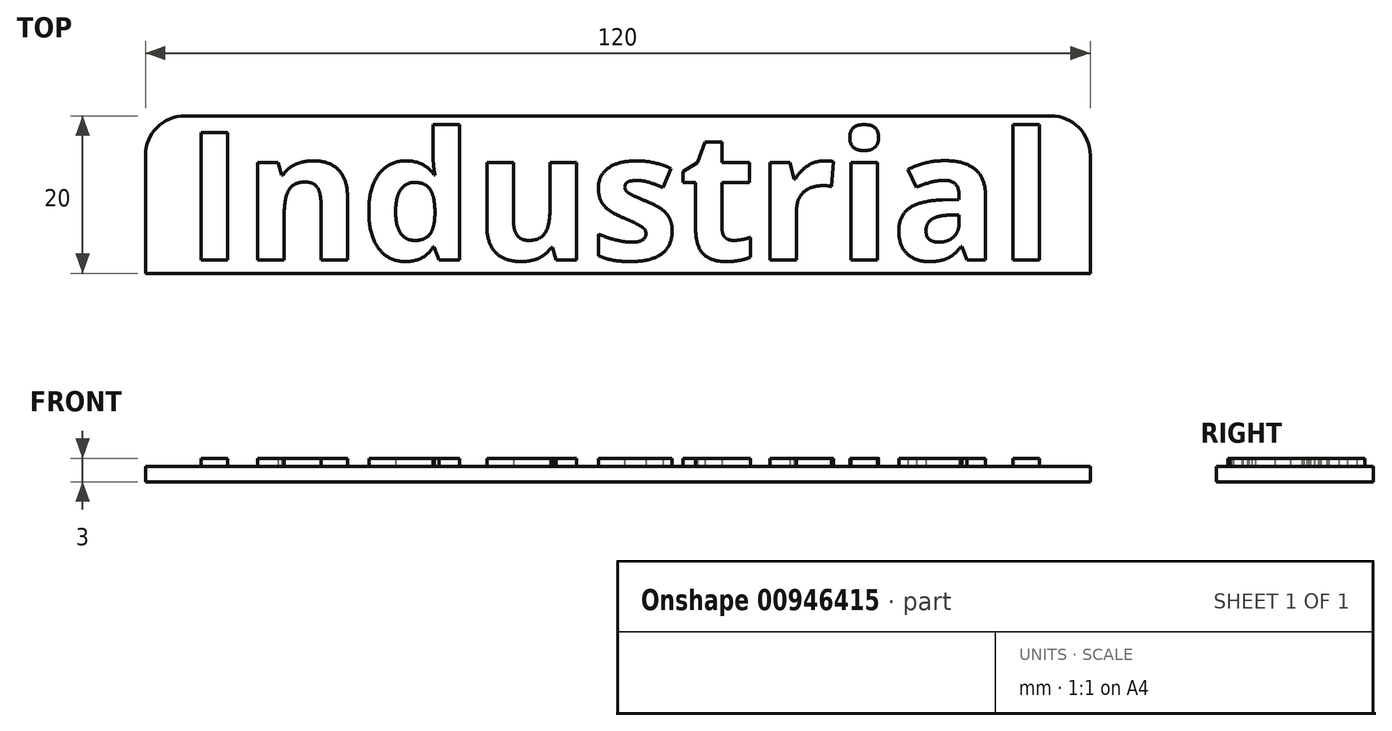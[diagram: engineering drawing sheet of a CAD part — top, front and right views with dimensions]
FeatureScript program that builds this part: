
annotation { "Feature Type Name" : "Feature", "Feature Type Description" : "" }
export const myFeature = defineFeature(function(context is Context, id is Id, definition is map)
    precondition{}
    {
        {
            var Q0;
            Q0=qCreatedBy(makeId("Top.planeOp"),FACE);
            var sketch = newSketch(context, id + "F0", { "sketchPlane" : qUnion([Q0])});
            skLineSegment(sketch, "E0.bottom", {"start": v(-60, 10) * mm, "end": v(60, 10) * mm});
            skLineSegment(sketch, "E0.top", {"start": v(-60, -10) * mm, "end": v(60, -10) * mm});
            skLineSegment(sketch, "E0.left", {"start": v(-60, 10) * mm, "end": v(-60, -10) * mm});
            skLineSegment(sketch, "E0.right", {"start": v(60, 10) * mm, "end": v(60, -10) * mm});
            skPoint(sketch, "E0.middle", {"position": v(0, 0) * mm});
            skSolve(sketch);
        }
        {
            var Q0;
            Q0=qSketchRegion(id+"F0",true);
            extrude(context, id + "F1", {"entities" : qUnion([Q0]), "depth" : 2 * mm, "offsetDistance" : 25 * mm});
        }
        {
            var Q0;
            Q0=makeQuery(id+"F1.opExtrude","CAP_FACE",FACE,{"disambiguationData":[OSD([sQuery(id+"F0.wireOp",EDGE,"E0.bottom"),sQuery(id+"F0.wireOp",EDGE,"E0.top"),sQuery(id+"F0.wireOp",EDGE,"E0.left"),sQuery(id+"F0.wireOp",EDGE,"E0.right")])],"isStart":false});
            var sketch = newSketch(context, id + "F2", { "sketchPlane" : qUnion([Q0])});
            skText(sketch, "E1", { "text": "Industrial\n", "fontName": "OpenSans-Bold.ttf"});
            const initialGuessF2  = {"E1": [-0.055, -0.00828, 1, 0, 0.01628]};
            skSetInitialGuess(sketch, initialGuessF2);
            skSolve(sketch);
        }
        {
            var Q0;
            Q0=qSketchRegion(id+"F2",true);
            extrude(context, id + "F3", {"entities" : qUnion([Q0]), "operationType" : NewBodyOperationType.ADD, "depth" : 1 * mm, "offsetDistance" : 25 * mm});
        }
        {
            var Q0;
            Q0=makeQuery(id+"F1.opExtrude","SWEPT_EDGE",EDGE,{"disambiguationData":[OSD([sQuery(id+"F0.wireOp",EDGE,"E0.bottom"),sQuery(id+"F0.wireOp",EDGE,"E0.left")])]});
            var Q1;
            Q1=makeQuery(id+"F1.opExtrude","SWEPT_EDGE",EDGE,{"disambiguationData":[OSD([sQuery(id+"F0.wireOp",EDGE,"E0.bottom"),sQuery(id+"F0.wireOp",EDGE,"E0.right")])]});
            fillet(context, id + "F4", {"entities" : qUnion([Q0, Q1]), "radius" : 5 * mm, "tangentPropagation" : true, "allowEdgeOverflow" : false});
        }
    });
